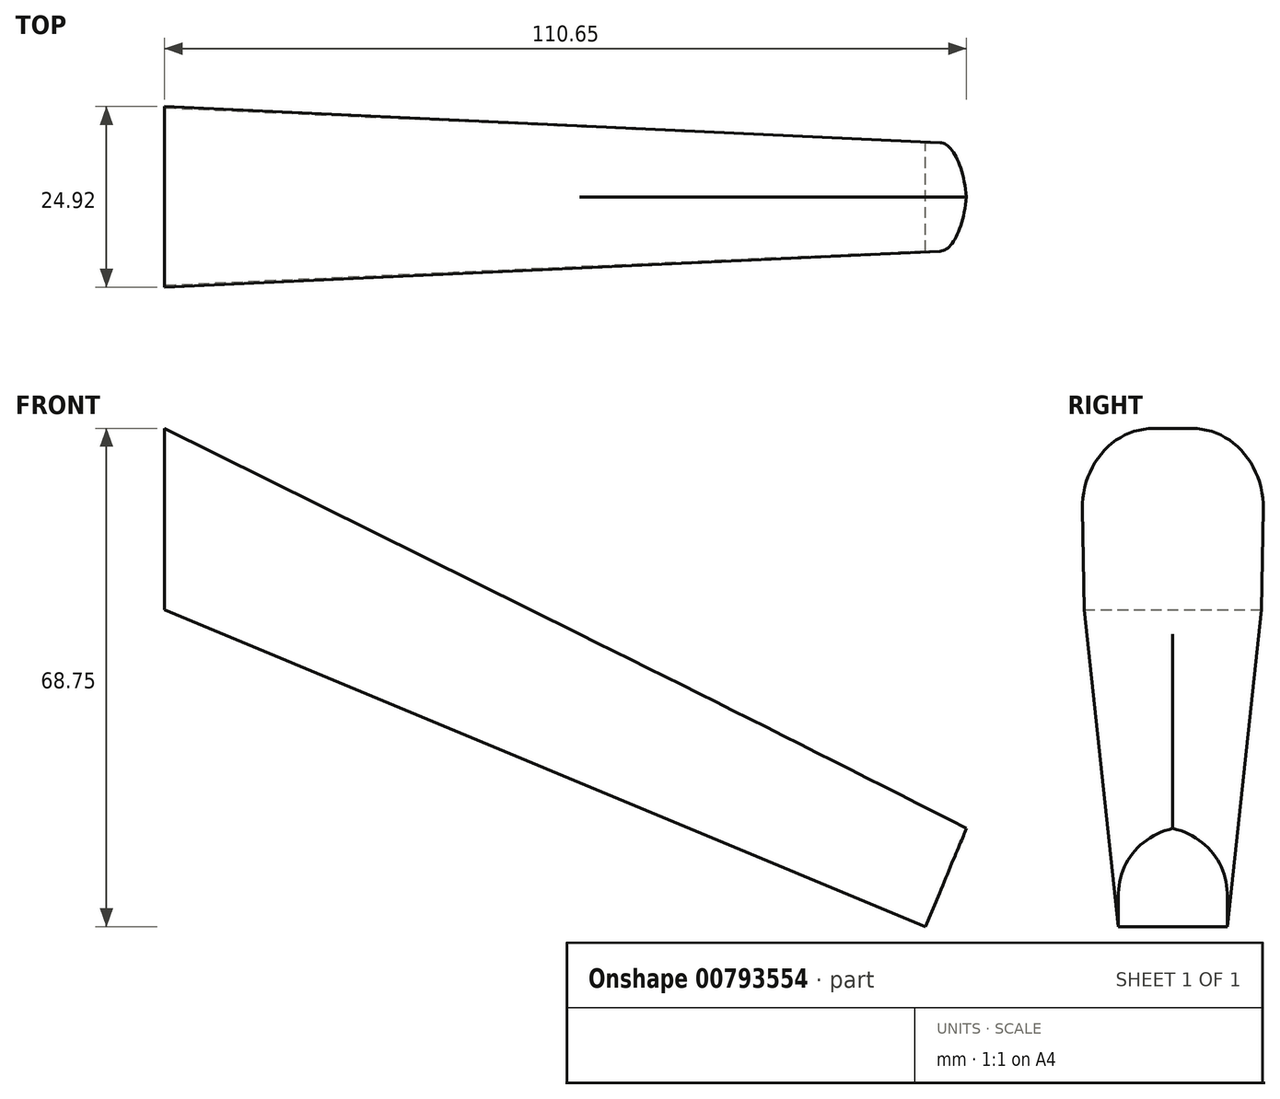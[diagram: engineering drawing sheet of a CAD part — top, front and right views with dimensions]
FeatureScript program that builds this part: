
annotation { "Feature Type Name" : "Feature", "Feature Type Description" : "" }
export const myFeature = defineFeature(function(context is Context, id is Id, definition is map)
    precondition{}
    {
        {
            var Q0;
            Q0=qCreatedBy(makeId("Front.planeOp"),FACE);
            var sketch = newSketch(context, id + "F0", { "sketchPlane" : qUnion([Q0])});
            skLineSegment(sketch, "E0", {"start": v(0, 0) * mm, "end": v(0, 620) * mm, "construction": true});
            skLineSegment(sketch, "E1", {"start": v(0, 620) * mm, "end": v(-300, 620) * mm, "construction": true});
            skLineSegment(sketch, "E2", {"start": v(-150, 620) * mm, "end": v(-150, 50) * mm, "construction": true});
            skLineSegment(sketch, "E3", {"start": v(-150, 0) * mm, "end": v(-30, 0) * mm, "construction": true});
            skLineSegment(sketch, "E4", {"start": v(-150, 50) * mm, "end": v(-30, 0) * mm});
            skLineSegment(sketch, "E5.0", {"start": v(-165, 620) * mm, "end": v(-165, 0) * mm});
            skLineSegment(sketch, "E6.0", {"start": v(-135, 620) * mm, "end": v(-135, 43.75) * mm});
            skLineSegment(sketch, "E7", {"start": v(-30, 0) * mm, "end": v(-24.23, 13.85) * mm});
            skLineSegment(sketch, "E8", {"start": v(-24.23, 13.85) * mm, "end": v(-138.55, 70.51) * mm});
            skLineSegment(sketch, "E9", {"start": v(-135, 43.75) * mm, "end": v(-135, 68.75) * mm, "construction": true});
            skSolve(sketch);
        }
        {
            var Q0;
            Q0 = qSketchRegion(id + "F0", true);
            extrude(context, id + "F1", {"entities" : qUnion([Q0]), "depth" : 25 * mm, "offsetDistance" : 25 * mm});
        }
        {
            var Q0;
            Q0=makeQuery(id+"F1.opExtrude","CAP_EDGE",EDGE,{"disambiguationData":[OSD([sQuery(id+"F0.wireOp",EDGE,"E7")])],"isStart":true});
            var Q1;
            Q1=makeQuery(id+"F1.opExtrude","CAP_EDGE",EDGE,{"disambiguationData":[OSD([sQuery(id+"F0.wireOp",EDGE,"E7")])],"isStart":false});
            chamfer(context, id + "F2", {"entities" : qUnion([Q0, Q1]), "chamferType" : ChamferType.TWO_OFFSETS, "width1" : 5 * mm, "oppositeDirection" : false, "width2" : 120 * mm, "tangentPropagation" : true});
        }
        {
            var Q0;
            Q0=makeQuery(id+"F1.opExtrude","SWEPT_EDGE",EDGE,{"disambiguationData":[OSD([sQuery(id+"F0.wireOp",EDGE,"E7"),sQuery(id+"F0.wireOp",EDGE,"E8")])]});
            var Q1;
            Q1=makeQuery(id+"F2.opChamfer","BLEND_EDGE",EDGE,{"blendedFrom":[makeQuery(id+"F1.opExtrude","CAP_EDGE",EDGE,{"disambiguationData":[OSD([sQuery(id+"F0.wireOp",EDGE,"E7")])],"isStart":false}),makeQuery(id+"F1.opExtrude","SWEPT_FACE",FACE,{"disambiguationData":[OSD([sQuery(id+"F0.wireOp",EDGE,"E8")])]})],"blendedInto":[makeQuery(id+"F1.opExtrude","SWEPT_FACE",FACE,{"disambiguationData":[OSD([sQuery(id+"F0.wireOp",EDGE,"E8")])]})]});
            var Q2;
            Q2=makeQuery(id+"F2.opChamfer","BLEND_EDGE",EDGE,{"blendedFrom":[makeQuery(id+"F1.opExtrude","CAP_EDGE",EDGE,{"disambiguationData":[OSD([sQuery(id+"F0.wireOp",EDGE,"E7")])],"isStart":true}),makeQuery(id+"F1.opExtrude","SWEPT_FACE",FACE,{"disambiguationData":[OSD([sQuery(id+"F0.wireOp",EDGE,"E8")])]})],"blendedInto":[makeQuery(id+"F1.opExtrude","SWEPT_FACE",FACE,{"disambiguationData":[OSD([sQuery(id+"F0.wireOp",EDGE,"E8")])]})]});
            fillet(context, id + "F3", {"entities" : qUnion([Q0, Q1, Q2]), "radius" : 10 * mm, "tangentPropagation" : true, "allowEdgeOverflow" : false});
        }
    });
